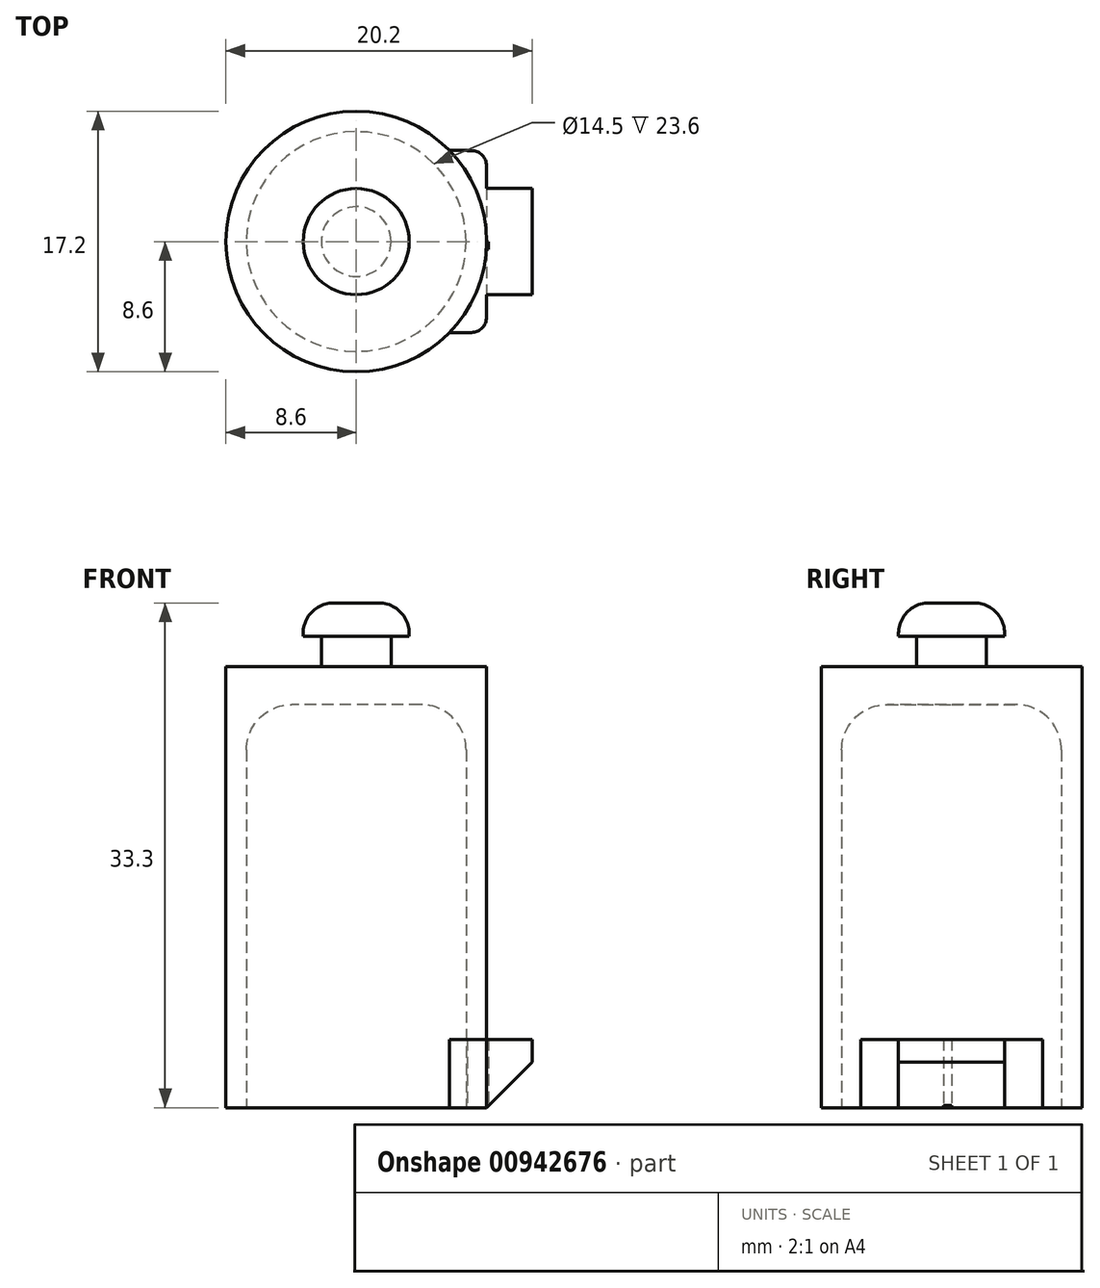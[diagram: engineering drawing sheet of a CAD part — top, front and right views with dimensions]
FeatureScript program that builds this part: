
annotation { "Feature Type Name" : "Feature", "Feature Type Description" : "" }
export const myFeature = defineFeature(function(context is Context, id is Id, definition is map)
    precondition{}
    {
        {
            var Q0;
            Q0=qCreatedBy(makeId("Top.planeOp"),FACE);
            var sketch = newSketch(context, id + "F0", { "sketchPlane" : qUnion([Q0])});
            skCircle(sketch, "E0", {"center": v(0, 0) * mm, "radius": 8.6 * mm});
            skCircle(sketch, "E1", {"center": v(0, 0) * mm, "radius": 7.25 * mm});
            skSolve(sketch);
        }
        {
            var Q0;
            Q0 = qSketchRegion(id + "F0", true);
            extrude(context, id + "F1", {"entities" : qUnion([Q0]), "depth" : 29.1 * mm, "offsetDistance" : 25 * mm});
        }
        {
            var Q0;
            Q0=makeQuery(id+"F1.opExtrude","CAP_FACE",FACE,{"disambiguationData":[OSD([sQuery(id+"F0.wireOp",EDGE,"E0"),sQuery(id+"F0.wireOp",EDGE,"E1")])],"isStart":false});
            var sketch = newSketch(context, id + "F2", { "sketchPlane" : qUnion([Q0])});
            skCircle(sketch, "E2", {"center": v(0, 0) * mm, "radius": 8.6 * mm});
            skSolve(sketch);
        }
        {
            var Q0;
            Q0 = qSketchRegion(id + "F2", true);
            extrude(context, id + "F3", {"entities" : qUnion([Q0]), "operationType" : NewBodyOperationType.ADD, "oppositeDirection" : true, "depth" : 2.5 * mm, "offsetDistance" : 25 * mm});
        }
        {
            var Q0;
            Q0=makeQuery(id+"F3.boolean.opBoolean","INTERSECT",EDGE,{"derivedFrom":[makeQuery(id+"F1.opExtrude","SWEPT_FACE",FACE,{"disambiguationData":[OSD([sQuery(id+"F0.wireOp",EDGE,"E1")])]}),makeQuery(id+"F3.opExtrude","CAP_FACE",FACE,{"disambiguationData":[OSD([sQuery(id+"F2.wireOp",EDGE,"E2")])],"isStart":false})]});
            fillet(context, id + "F4", {"entities" : qUnion([Q0]), "radius" : 3 * mm, "tangentPropagation" : true, "allowEdgeOverflow" : false});
        }
        {
            var Q0;
            Q0=makeQuery(id+"F3.boolean.opBoolean","MERGE",FACE,{"derivedFrom":[makeQuery(id+"F1.opExtrude","CAP_FACE",FACE,{"disambiguationData":[OSD([sQuery(id+"F0.wireOp",EDGE,"E0"),sQuery(id+"F0.wireOp",EDGE,"E1")])],"isStart":false}),makeQuery(id+"F3.opExtrude","CAP_FACE",FACE,{"disambiguationData":[OSD([sQuery(id+"F2.wireOp",EDGE,"E2")])],"isStart":true})]});
            var sketch = newSketch(context, id + "F5", { "sketchPlane" : qUnion([Q0])});
            skCircle(sketch, "E3", {"center": v(0, 0) * mm, "radius": 2.3 * mm});
            skSolve(sketch);
        }
        {
            var Q0;
            Q0 = qSketchRegion(id + "F5", true);
            extrude(context, id + "F6", {"entities" : qUnion([Q0]), "operationType" : NewBodyOperationType.ADD, "depth" : 2 * mm, "offsetDistance" : 25 * mm});
        }
        {
            var Q0;
            Q0 = qSketchRegion(id + "F5", true);
            extrude(context, id + "F7", {"entities" : qUnion([Q0]), "operationType" : NewBodyOperationType.ADD, "oppositeDirection" : true, "depth" : 2 * mm, "offsetDistance" : 25 * mm});
        }
        {
            var Q0;
            Q0=makeQuery(id+"F6.opExtrude","CAP_FACE",FACE,{"disambiguationData":[OSD([sQuery(id+"F5.wireOp",EDGE,"E3")])],"isStart":false});
            var sketch = newSketch(context, id + "F8", { "sketchPlane" : qUnion([Q0])});
            skCircle(sketch, "E4", {"center": v(0, 0) * mm, "radius": 3.5 * mm});
            skSolve(sketch);
        }
        {
            var Q0;
            Q0 = qSketchRegion(id + "F8", true);
            extrude(context, id + "F9", {"entities" : qUnion([Q0]), "operationType" : NewBodyOperationType.ADD, "depth" : 2.2 * mm, "offsetDistance" : 25 * mm});
        }
        {
            var Q0;
            Q0=makeQuery(id+"F9.opExtrude","CAP_EDGE",EDGE,{"disambiguationData":[OSD([sQuery(id+"F8.wireOp",EDGE,"E4")])],"isStart":false});
            fillet(context, id + "F10", {"entities" : qUnion([Q0]), "radius" : 2 * mm, "tangentPropagation" : true, "allowEdgeOverflow" : false});
        }
        {
            var Q0;
            Q0=makeQuery(id+"F1.opExtrude","CAP_FACE",FACE,{"disambiguationData":[OSD([sQuery(id+"F0.wireOp",EDGE,"E0"),sQuery(id+"F0.wireOp",EDGE,"E1")])],"isStart":true});
            var sketch = newSketch(context, id + "F11", { "sketchPlane" : qUnion([Q0])});
            skLineSegment(sketch, "E5.bottom", {"start": v(8.6, 0) * mm, "end": v(7.34, 0) * mm});
            skLineSegment(sketch, "E5.top", {"start": v(8.6, 6) * mm, "end": v(7.34, 6) * mm});
            skLineSegment(sketch, "E5.left", {"start": v(8.6, 0) * mm, "end": v(8.6, 6) * mm});
            skLineSegment(sketch, "E5.right", {"start": v(7.34, 0) * mm, "end": v(7.34, 6) * mm});
            skLineSegment(sketch, "E6.bottom", {"start": v(7.34, 0) * mm, "end": v(8.6, 0) * mm});
            skLineSegment(sketch, "E6.top", {"start": v(7.34, -6) * mm, "end": v(8.6, -6) * mm});
            skLineSegment(sketch, "E6.left", {"start": v(7.34, 0) * mm, "end": v(7.34, -6) * mm});
            skLineSegment(sketch, "E6.right", {"start": v(8.6, 0) * mm, "end": v(8.6, -6) * mm});
            skLineSegment(sketch, "E7.bottom", {"start": v(7.34, 6) * mm, "end": v(6.15, 6) * mm});
            skLineSegment(sketch, "E7.top", {"start": v(7.34, -6) * mm, "end": v(6.15, -6) * mm});
            skLineSegment(sketch, "E7.left", {"start": v(7.34, 6) * mm, "end": v(7.34, -6) * mm});
            skLineSegment(sketch, "E7.right", {"start": v(6.15, 6) * mm, "end": v(6.15, 3.87) * mm});
            skArc(sketch, "E8", {"start": v(6.15, -3.87) * mm, "mid": v(7.27, 0) * mm, "end": v(6.15, 3.87) * mm});
            skLineSegment(sketch, "E9.trimOffspring", {"start": v(6.15, -3.87) * mm, "end": v(6.15, -6) * mm});
            skLineSegment(sketch, "E10.bottom", {"start": v(8.6, 0) * mm, "end": v(11.6, 0) * mm});
            skLineSegment(sketch, "E10.top", {"start": v(8.6, -3.5) * mm, "end": v(11.6, -3.5) * mm});
            skLineSegment(sketch, "E10.left", {"start": v(8.6, 0) * mm, "end": v(8.6, -3.5) * mm});
            skLineSegment(sketch, "E10.right", {"start": v(11.6, 0) * mm, "end": v(11.6, -3.5) * mm});
            skLineSegment(sketch, "E11.bottom", {"start": v(8.6, 0) * mm, "end": v(8.73, 0) * mm});
            skLineSegment(sketch, "E11.top", {"start": v(8.6, 0.53) * mm, "end": v(8.73, 0.53) * mm});
            skLineSegment(sketch, "E11.left", {"start": v(8.6, 0) * mm, "end": v(8.6, 0.53) * mm});
            skLineSegment(sketch, "E11.right", {"start": v(8.73, 0) * mm, "end": v(8.73, 0.53) * mm});
            skLineSegment(sketch, "E12.bottom", {"start": v(11.6, 3.5) * mm, "end": v(8.6, 3.5) * mm});
            skLineSegment(sketch, "E12.top", {"start": v(11.6, 0) * mm, "end": v(8.6, 0) * mm});
            skLineSegment(sketch, "E12.left", {"start": v(11.6, 3.5) * mm, "end": v(11.6, 0) * mm});
            skLineSegment(sketch, "E12.right", {"start": v(8.6, 3.5) * mm, "end": v(8.6, 0) * mm});
            skSolve(sketch);
        }
        {
            var Q0;
            Q0 = qSketchRegion(id + "F11", true);
            extrude(context, id + "F12", {"entities" : qUnion([Q0]), "operationType" : NewBodyOperationType.ADD, "oppositeDirection" : true, "depth" : 4.5 * mm, "offsetDistance" : 25 * mm});
        }
        {
            var Q0;
            Q0=makeQuery(id+"F12.opExtrude","CAP_EDGE",EDGE,{"disambiguationData":[OSD([sQuery(id+"F11.wireOp",EDGE,"E10.right"),sQuery(id+"F11.wireOp",EDGE,"E12.left")])],"isStart":true});
            chamfer(context, id + "F13", {"entities" : qUnion([Q0]), "width" : 3 * mm, "tangentPropagation" : true});
        }
        {
            var Q0;
            Q0=makeQuery(id+"F12.opExtrude","SWEPT_EDGE",EDGE,{"disambiguationData":[OSD([sQuery(id+"F11.wireOp",EDGE,"E6.top"),sQuery(id+"F11.wireOp",EDGE,"E6.right")])]});
            var Q1;
            Q1=makeQuery(id+"F12.opExtrude","SWEPT_EDGE",EDGE,{"disambiguationData":[OSD([sQuery(id+"F11.wireOp",EDGE,"E5.top"),sQuery(id+"F11.wireOp",EDGE,"E5.left")])]});
            fillet(context, id + "F14", {"entities" : qUnion([Q0, Q1]), "radius" : 1 * mm, "tangentPropagation" : true, "allowEdgeOverflow" : false});
        }
    });
